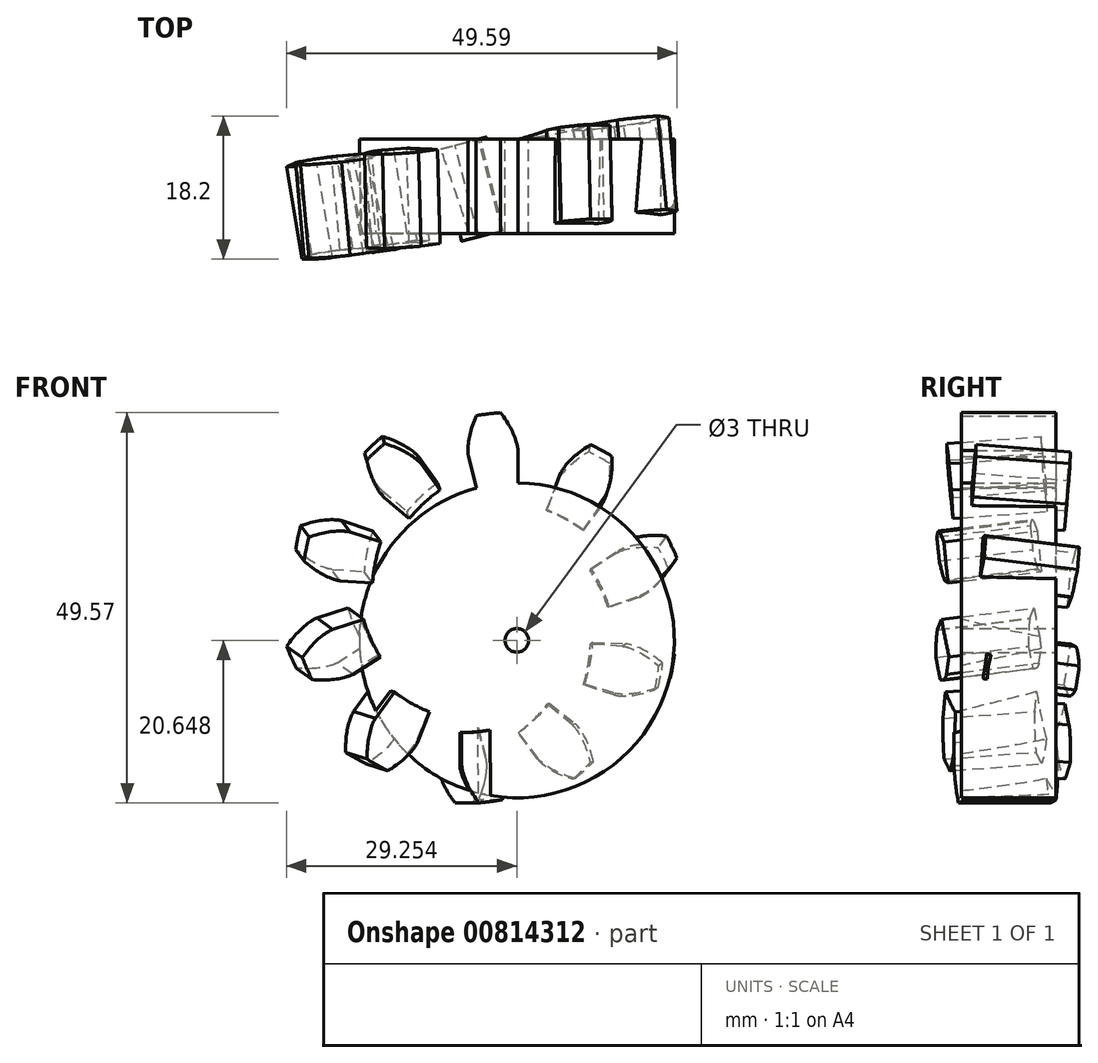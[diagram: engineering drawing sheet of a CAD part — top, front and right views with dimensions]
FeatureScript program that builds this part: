
annotation { "Feature Type Name" : "Feature", "Feature Type Description" : "" }
export const myFeature = defineFeature(function(context is Context, id is Id, definition is map)
    precondition{}
    {
        {
            assignVariable(context, id + "F0", {"name" : "numberOfTeeth", "anyValue" : 10});
        }
        {
            assignVariable(context, id + "F1", {"name" : "thickness", "anyValue" : 12});
        }
        {
            var Q0;
            Q0=qCreatedBy(makeId("Front.planeOp"),FACE);
            var sketch = newSketch(context, id + "F2", { "sketchPlane" : qUnion([Q0])});
            skCircle(sketch, "E0", {"center": v(-37.02, 31.5) * mm, "radius": 25 * mm, "construction": true});
            skLineSegment(sketch, "E1", {"start": v(-37.02, 31.5) * mm, "end": v(-37.02, 66.5) * mm, "construction": true});
            skPoint(sketch, "E2", {"position": v(-37.02, 56.5) * mm});
            skLineSegment(sketch, "E3", {"start": v(-66.46, 56.5) * mm, "end": v(-7.57, 56.5) * mm, "construction": true});
            skLineSegment(sketch, "E4", {"start": v(-64.29, 49.2) * mm, "end": v(-9.74, 63.82) * mm, "construction": true});
            skLineSegment(sketch, "E5", {"start": v(-37.02, 31.5) * mm, "end": v(-43.27, 54.83) * mm, "construction": true});
            skCircle(sketch, "E6", {"center": v(-37.02, 31.5) * mm, "radius": 24.15 * mm, "construction": true});
            skArc(sketch, "E7", {"start": v(-43.27, 54.83) * mm, "mid": v(-47.74, 53.14) * mm, "end": v(-51.8, 50.6) * mm, "construction": true});
            skLineSegment(sketch, "E8", {"start": v(-51.8, 50.6) * mm, "end": v(-37.02, 31.5) * mm, "construction": true});
            skLineSegment(sketch, "E9", {"start": v(-51.8, 50.6) * mm, "end": v(-39.1, 60.43) * mm, "construction": true});
            skArc(sketch, "E10", {"start": v(-43.27, 54.83) * mm, "mid": v(-41.56, 55.22) * mm, "end": v(-39.84, 55.5) * mm, "construction": true});
            skLineSegment(sketch, "E11", {"start": v(-39.84, 55.5) * mm, "end": v(-37.02, 31.5) * mm, "construction": true});
            skLineSegment(sketch, "E12", {"start": v(-39.84, 55.5) * mm, "end": v(-36.88, 55.84) * mm, "construction": true});
            skArc(sketch, "E13", {"start": v(-36.87, 55.66) * mm, "mid": v(-40.1, 55.46) * mm, "end": v(-43.27, 54.83) * mm, "construction": true});
            skArc(sketch, "E14", {"start": v(-41.87, 55.16) * mm, "mid": v(-42.57, 55) * mm, "end": v(-43.27, 54.83) * mm, "construction": true});
            skLineSegment(sketch, "E15", {"start": v(-41.87, 55.16) * mm, "end": v(-37.02, 31.5) * mm, "construction": true});
            skLineSegment(sketch, "E16", {"start": v(-41.87, 55.16) * mm, "end": v(-36.94, 56.18) * mm, "construction": true});
            skArc(sketch, "E17", {"start": v(-43.27, 54.83) * mm, "mid": v(-42.93, 54.92) * mm, "end": v(-42.59, 55) * mm});
            skLineSegment(sketch, "E18", {"start": v(-42.59, 55) * mm, "end": v(-37.02, 31.5) * mm, "construction": true});
            skLineSegment(sketch, "E19", {"start": v(-42.59, 55) * mm, "end": v(-36.97, 56.34) * mm, "construction": true});
            skArc(sketch, "E20", {"start": v(-43.27, 54.83) * mm, "mid": v(-42.13, 55.1) * mm, "end": v(-41, 55.33) * mm});
            skLineSegment(sketch, "E21", {"start": v(-41, 55.33) * mm, "end": v(-37.02, 31.5) * mm, "construction": true});
            skLineSegment(sketch, "E22", {"start": v(-41, 55.33) * mm, "end": v(-36.9, 56) * mm, "construction": true});
            skArc(sketch, "E23", {"start": v(-43.27, 54.83) * mm, "mid": v(-46.66, 53.65) * mm, "end": v(-49.83, 51.97) * mm});
            skLineSegment(sketch, "E24", {"start": v(-49.83, 51.97) * mm, "end": v(-37.02, 31.5) * mm, "construction": true});
            skLineSegment(sketch, "E25", {"start": v(-49.83, 51.97) * mm, "end": v(-38.26, 59.22) * mm, "construction": true});
            skArc(sketch, "E26", {"start": v(-43.27, 54.83) * mm, "mid": v(-45.55, 54.1) * mm, "end": v(-47.74, 53.14) * mm});
            skLineSegment(sketch, "E27", {"start": v(-47.74, 53.14) * mm, "end": v(-37.02, 31.5) * mm, "construction": true});
            skLineSegment(sketch, "E28", {"start": v(-47.74, 53.14) * mm, "end": v(-37.65, 58.15) * mm, "construction": true});
            skArc(sketch, "E29", {"start": v(-43.27, 54.83) * mm, "mid": v(-44.42, 54.5) * mm, "end": v(-45.55, 54.1) * mm});
            skLineSegment(sketch, "E30", {"start": v(-45.55, 54.1) * mm, "end": v(-37.02, 31.5) * mm, "construction": true});
            skLineSegment(sketch, "E31", {"start": v(-45.55, 54.1) * mm, "end": v(-37.25, 57.23) * mm, "construction": true});
            skLineSegment(sketch, "E32", {"start": v(-39.1, 60.43) * mm, "end": v(-37.02, 31.5) * mm, "construction": true});
            skSolve(sketch);
        }
        {
            var Q0;
            Q0=qCreatedBy(makeId("Front.planeOp"),FACE);
            var sketch = newSketch(context, id + "F3", { "sketchPlane" : qUnion([Q0])});
            skPoint(sketch, "E33", {"position": v(-37.02, 56.5) * mm});
            skPoint(sketch, "E34", {"position": v(-37.02, 31.5) * mm});
            skLineSegment(sketch, "E35", {"start": v(-37.02, 31.5) * mm, "end": v(-41.28, 65.24) * mm, "construction": true});
            skCircle(sketch, "E36", {"center": v(-37.02, 31.5) * mm, "radius": 24.15 * mm, "construction": true});
            skPoint(sketch, "E37", {"position": v(-37.02, 65.5) * mm});
            skLineSegment(sketch, "E38", {"start": v(-37.02, 65.5) * mm, "end": v(-37.02, 31.5) * mm, "construction": true});
            skCircle(sketch, "E39", {"center": v(-37.02, 31.5) * mm, "radius": 20 * mm, "construction": true});
            skPoint(sketch, "E40.0", {"position": v(-37.65, 58.15) * mm});
            skPoint(sketch, "E41.0", {"position": v(-37.25, 57.23) * mm});
            skPoint(sketch, "E42.0", {"position": v(-38.26, 59.22) * mm});
            skPoint(sketch, "E43.0", {"position": v(-36.97, 56.34) * mm});
            skPoint(sketch, "E44.0", {"position": v(-36.94, 56.18) * mm});
            skPoint(sketch, "E45.0", {"position": v(-36.9, 56) * mm});
            skPoint(sketch, "E46.0", {"position": v(-36.88, 55.84) * mm});
            skPoint(sketch, "E47.0", {"position": v(-36.87, 55.66) * mm});
            skPoint(sketch, "E48.0", {"position": v(-39.1, 60.43) * mm});
            skFitSpline(sketch, "E49", {"points": [v(-36.87, 55.66) * mm, v(-36.88, 55.84) * mm, v(-36.9, 56) * mm, v(-36.94, 56.18) * mm, v(-36.97, 56.34) * mm, v(-37.02, 56.5) * mm, v(-37.25, 57.23) * mm, v(-37.65, 58.15) * mm, v(-38.26, 59.22) * mm, v(-39.1, 60.43) * mm], "startDerivative": vector(-2.23, 7.56) * mm, "endDerivative": vector(-3.5, 4.82) * mm});
            skArc(sketch, "E50", {"start": v(-39.1, 60.43) * mm, "mid": v(-39.88, 60.37) * mm, "end": v(-40.65, 60.28) * mm});
            skFitSpline(sketch, "E51.MirrorCS", {"points": [v(-43.17, 54.86) * mm, v(-43.2, 55.04) * mm, v(-43.22, 55.21) * mm, v(-43.23, 55.38) * mm, v(-43.23, 55.55) * mm, v(-43.23, 55.72) * mm, v(-43.19, 56.48) * mm, v(-43.03, 57.47) * mm, v(-42.7, 58.66) * mm, v(-42.19, 60.04) * mm], "startDerivative": vector(0.28, 7.87) * mm, "endDerivative": vector(2.2, 5.54) * mm});
            skArc(sketch, "E52.MirrorCS", {"start": v(-42.19, 60.04) * mm, "mid": v(-41.42, 60.17) * mm, "end": v(-40.65, 60.28) * mm});
            skLineSegment(sketch, "E53", {"start": v(-36.87, 55.66) * mm, "end": v(-36.87, 51.5) * mm});
            skArc(sketch, "E54", {"start": v(-36.87, 51.5) * mm, "mid": v(-38.2, 51.47) * mm, "end": v(-39.52, 51.35) * mm});
            skLineSegment(sketch, "E55.MirrorCS", {"start": v(-43.17, 54.86) * mm, "end": v(-42.13, 50.84) * mm});
            skArc(sketch, "E56.MirrorCS", {"start": v(-42.13, 50.84) * mm, "mid": v(-40.84, 51.14) * mm, "end": v(-39.52, 51.35) * mm});
            skSolve(sketch);
        }
        {
            var Q0;
            Q0=qCreatedBy(makeId("Front.planeOp"),FACE);
            var sketch = newSketch(context, id + "F4", { "sketchPlane" : qUnion([Q0])});
            skCircle(sketch, "E57.0", {"center": v(-37.02, 31.5) * mm, "radius": 20 * mm});
            skFitSpline(sketch, "E58.1.0", {"points": [v(-39.44, 58.37) * mm, v(-39.55, 58.09) * mm, v(-39.7, 57.8) * mm, v(-39.9, 57.19) * mm, v(-40.05, 56.7) * mm, v(-40.15, 56.26) * mm, v(-40.18, 56.02) * mm, v(-40.21, 55.78) * mm, v(-40.23, 55.57) * mm, v(-40.25, 55.25) * mm, v(-40.2, 55.32) * mm, v(-40.22, 55.07) * mm]});
            skLineSegment(sketch, "E58.1.1", {"start": v(-43.17, 54.86) * mm, "end": v(-42.13, 50.84) * mm});
            skArc(sketch, "E58.1.2", {"start": v(-42.13, 50.84) * mm, "mid": v(-40.84, 51.14) * mm, "end": v(-39.52, 51.35) * mm});
            skArc(sketch, "E58.1.3", {"start": v(-39.52, 51.35) * mm, "mid": v(-38.2, 51.47) * mm, "end": v(-36.87, 51.5) * mm});
            skLineSegment(sketch, "E58.1.4", {"start": v(-36.87, 51.5) * mm, "end": v(-36.87, 55.66) * mm});
            skFitSpline(sketch, "E58.1.5", {"points": [v(-36.75, 55.36) * mm, v(-36.8, 55.6) * mm, v(-36.75, 55.54) * mm, v(-36.82, 55.86) * mm, v(-36.87, 56.06) * mm, v(-36.94, 56.29) * mm, v(-37.02, 56.51) * mm, v(-37.19, 56.94) * mm, v(-37.4, 57.4) * mm, v(-37.7, 57.96) * mm, v(-37.9, 58.22) * mm, v(-38.06, 58.48) * mm]});
            skArc(sketch, "E58.1.6", {"start": v(-39.1, 60.43) * mm, "mid": v(-39.88, 60.37) * mm, "end": v(-40.65, 60.28) * mm});
            skArc(sketch, "E58.1.7", {"start": v(-40.65, 60.28) * mm, "mid": v(-41.42, 60.17) * mm, "end": v(-42.19, 60.04) * mm});
            skSolve(sketch);
        }
        {
            var Q0;
            {var subQ0=sQuery(id+"F4.wireOp",EDGE,"E57.0");var subQ1=makeQuery(id+"F4.imprint","INTERSECT",VERTEX,{"derivedFrom":[subQ0,sQuery(id+"F4.wireOp",EDGE,"E58.1.1")]});Q0=makeQuery(id+"F4.imprint","IMPRINT",FACE,{"disambiguationData":[TD([[makeQuery(id+"F4.imprint","IMPRINT",EDGE,{"disambiguationData":[TD([[subQ1,1.0]])],"derivedFrom":subQ0}),1.0]])]});}
            extrude(context, id + "F5", {"entities" : qUnion([Q0]), "depth" : (getVariable(context, 'thickness')) * mm, "offsetDistance" : 25 * mm});
        }
        {
            var Q0;
            Q0=makeQuery(id+"F3.imprint","IMPRINT",FACE,{"disambiguationData":[TD([[makeQuery(id+"F3.imprint","IMPRINT",EDGE,{"derivedFrom":sQuery(id+"F3.wireOp",EDGE,"E49")}),1.0]])]});
            extrude(context, id + "F6", {"entities" : qUnion([Q0]), "depth" : (getVariable(context, 'thickness')) * mm, "offsetDistance" : 25 * mm});
        }
        {
            var Q0;
            Q0=makeQuery(id+"F6.opExtrude","CAP_EDGE",EDGE,{"disambiguationData":[OSD([sQuery(id+"F3.wireOp",EDGE,"E50"),sQuery(id+"F3.wireOp",EDGE,"E52.MirrorCS")])],"isStart":false});
            cPoint(context, id + "F7", {"entities" : qUnion([Q0]), "parameter" : 0.5});
        }
        {
            var Q0;
            Q0=qCreatedBy(id+"F7",VERTEX);
            var Q1;
            Q1=sQuery(id+"F3.wireOp",VERTEX,"E52.MirrorCS.end");
            var Q2;
            Q2=sQuery(id+"F3.wireOp",VERTEX,"E56.MirrorCS.end");
            cPlane(context, id + "F8", {"entities" : qUnion([Q0, Q1, Q2]), "cplaneType" : CPlaneType.THREE_POINT, "offset" : 0 * mm, "width" : 150 * mm, "height" : 150 * mm});
        }
        {
            var Q0;
            Q0=qCreatedBy(id+"F8.planeOp",FACE);
            var sketch = newSketch(context, id + "F9", { "sketchPlane" : qUnion([Q0])});
            skPoint(sketch, "E59.0", {"position": v(0, 35.9) * mm});
            skLineSegment(sketch, "E60", {"start": v(0, 35.9) * mm, "end": v(30.78, 35.9) * mm, "construction": true});
            skSolve(sketch);
        }
        {
            var Q0;
            Q0=makeQuery(id+"F6.opExtrude","SWEPT_BODY",BODY,{"disambiguationData":[OSD([sQuery(id+"F3.wireOp",EDGE,"E49"),sQuery(id+"F3.wireOp",EDGE,"E50"),sQuery(id+"F3.wireOp",EDGE,"E51.MirrorCS"),sQuery(id+"F3.wireOp",EDGE,"E52.MirrorCS"),sQuery(id+"F3.wireOp",EDGE,"E53"),sQuery(id+"F3.wireOp",EDGE,"E54"),sQuery(id+"F3.wireOp",EDGE,"E55.MirrorCS"),sQuery(id+"F3.wireOp",EDGE,"E56.MirrorCS")])]});
            var Q1;
            Q1=sQuery(id+"F9.wireOp",EDGE,"E60");
            circularPattern(context, id + "F10", {"operationType" : NewBodyOperationType.ADD, "entities" : qUnion([Q0]), "axis" : qUnion([Q1]), "angle" : 360 * degree, "instanceCount" : getVariable(context, 'numberOfTeeth'), "equalSpace" : true});
        }
        {
            var Q0;
            Q0=qCreatedBy(makeId("Front.planeOp"),FACE);
            var sketch = newSketch(context, id + "F11", { "sketchPlane" : qUnion([Q0])});
            skPoint(sketch, "E61.0", {"position": v(-37.02, 31.5) * mm});
            skCircle(sketch, "E62", {"center": v(-37.02, 31.5) * mm, "radius": 1.5 * mm});
            skSolve(sketch);
        }
        {
            var Q0;
            Q0=makeQuery(id+"F11.imprint","IMPRINT",FACE,{"disambiguationData":[TD([[makeQuery(id+"F11.imprint","IMPRINT",EDGE,{"derivedFrom":sQuery(id+"F11.wireOp",EDGE,"E62")}),1.0]])]});
            extrude(context, id + "F12", {"entities" : qUnion([Q0]), "operationType" : NewBodyOperationType.REMOVE, "depth" : (getVariable(context, 'thickness')) * mm, "offsetDistance" : 25 * mm});
        }
    });
